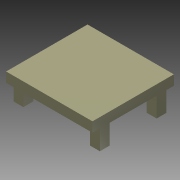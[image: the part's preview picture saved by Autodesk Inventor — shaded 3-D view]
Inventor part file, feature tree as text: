
AUTODESK INVENTOR PART (.ipt)
format: ipt  version: 2015 (Build 190159000, 159)  size: 593,408 bytes
history: native  units: in
note: dims shown in document units (in); Inventor stores cm internally (conversion verified against a paired STEP export)
features: thread x33, other x13, sketch x10, plane x6, projected_geometry x6, extrude x5, hole x4, mirror x3, pattern_circular x1, fillet x1, boolean_combine x1
ambient origin geometry x8: Origin, YZ Plane, XZ Plane, XY Plane, X Axis, Y Axis, Z Axis, Center Point
bodies: Solid6 (feature_tree)
feature tree (83):
  other  "board_with_hole_pipes.ipt"
  other  "Layout with const "
  plane  "Work Plane1"
  extrude  "Extrusion1"  Depth=18.0in
  extrude  "Extrusion2"  Depth=23.5in
  hole  "Hole1"  [1 undecoded]
  thread  "Thread1"  [1 undecoded]
  pattern_circular  "Circular Pattern1"  [2 undecoded]
  fillet  "Fillet1"  Radius=3.0in
  plane  "Work Plane3"
  hole  "Hole2"  [1 undecoded]
  thread  "Thread2"  [1 undecoded]
  thread  "Thread3"  [1 undecoded]
  thread  "Thread4"  [1 undecoded]
  thread  "Thread5"  [1 undecoded]
  thread  "Thread6"  [1 undecoded]
  thread  "Thread7"  [1 undecoded]
  mirror  "Mirror1"
  mirror  "Mirror2"
  mirror  "Mirror3"
  plane  "Work Plane4"
  extrude  "Extrusion3"  Depth=0.25in
  thread  "Thread8"  [1 undecoded]
  thread  "Thread9"  [1 undecoded]
  thread  "Thread10"  [1 undecoded]
  thread  "Thread11"  [1 undecoded]
  thread  "Thread12"  [1 undecoded]
  thread  "Thread13"  [1 undecoded]
  thread  "Thread14"  [1 undecoded]
  thread  "Thread15"  [1 undecoded]
  thread  "Thread16"  [1 undecoded]
  thread  "Thread17"  [1 undecoded]
  thread  "Thread18"  [1 undecoded]
  thread  "Thread19"  [1 undecoded]
  thread  "Thread20"  [1 undecoded]
  thread  "Thread21"  [1 undecoded]
  thread  "Thread22"  [1 undecoded]
  thread  "Thread23"  [1 undecoded]
  thread  "Thread24"  [1 undecoded]
  thread  "Thread25"  [1 undecoded]
  extrude  "Extrusion4"  Depth=0.25in TaperAngle=0.0deg
  plane  "Work Plane7"
  extrude  "Extrusion5"  Depth=0.25in TaperAngle=0.0deg
  boolean_combine  "Combine1"
  plane  "Work Plane8"
  plane  "Work Plane9"
  hole  "Hole3"  [1 undecoded]
  hole  "Hole4"  [1 undecoded]
  thread  "Thread26"  [1 undecoded]
  thread  "Thread27"  [1 undecoded]
  thread  "Thread28"  [1 undecoded]
  thread  "Thread29"  [1 undecoded]
  thread  "Thread30"  [1 undecoded]
  thread  "Thread31"  [1 undecoded]
  thread  "Thread32"  [1 undecoded]
  thread  "Thread33"  [1 undecoded]
  other  "Solid1::board_with_hole_pipes.ipt"
  other  "TaggingFeature1"
  sketch  "Sketch3"  dims[d0=0.1969in d1=18.0in]
  sketch  "Sketch4"  dims[d2=24.0in d3=23.5in]
  other  "legFL"
  sketch  "Sketch5"  dims[d4=17.5in d5=5.5in d6=1.5in]
  sketch  "Sketch6"  dims[d9=5.5in]
  sketch  "Sketch7"  dims[d10=1.5in]
  other  "Pattern of legFL:1"
  other  "legFR"
  other  "Pattern of legFL:2"
  other  "legBR"
  other  "Pattern of legFR:3"
  other  "legBL"
  sketch  "Sketch8"  dims[d11=5.5in]
  projected_geometry  "Projected Loop2"
  sketch  "Sketch10"  dims[d12=1.5in]
  sketch  "Sketch11"  dims[d15=4.0in]
  other  "miniplat"
  sketch  "Sketch12"  dims[d18=5.5in]
  projected_geometry  "Projected Loop3"
  projected_geometry  "Projected Loop4"
  projected_geometry  "Projected Loop5"
  projected_geometry  "Projected Loop6"
  projected_geometry  "Projected Loop7"
  sketch  "Sketch13"  dims[d19=1.5in d22=5.0in d23=3.0in d24=5.0in d25=3.0in d26=3.0in d27=3.0in d28=3.0in d29=5.0in d30=4.0in d31=3.5in d32=0.5in d33=1.0in d34=0.0in d35=0.0in d36=5.0in d37=0.5in d38=0.0in d39=0.25in d40=0.75in d41=0.375in d42=0.25in d43=0.5635in d44=1.8125in d45=0.8108in d46=1.0in d47=0.0in d48=2.3622in d49=360.0deg d51=0.4375in d52=0.25in d53=0.75in d54=0.375in d55=0.25in d56=0.5635in d57=1.8125in d58=0.8108in d59=1.0in d60=0.0in d61=1.0in d62=0.0in d63=1.0in d64=0.0in d65=1.0in d66=0.0in d67=1.0in d68=0.0in d69=1.0in d70=0.0in d71=3.475in d72=0.0in d73=1.0in d74=0.0in d75=1.0in d76=0.0in d77=1.0in d78=0.0in d79=1.0in d80=0.0in d81=1.0in d82=0.0in d83=1.0in d84=0.0in d85=1.0in d86=0.0in d87=1.0in d88=0.0in d89=1.0in d90=0.0in d91=1.0in d92=0.0in d93=1.0in d94=0.0in d95=1.0in d96=0.0in d97=1.0in d98=0.0in d99=1.0in d100=0.0in d101=1.0in d102=0.0in d103=1.0in d104=0.0in d105=1.0in d106=0.0in d107=1.0in d108=0.0in d109=1.0in d110=1.0in d111=1.0in d112=1.0in d113=1.0in d114=1.0in d115=2.0in d116=0.0in d117=1.0in d118=0.0in d119=0.5in d120=0.5in d121=0.5in d122=0.5in d123=0.5in d124=0.75in d125=0.375in d126=0.25in d127=0.5635in d128=2.0in d129=0.0in d130=0.5in d131=0.75in d132=0.375in d133=0.25in d134=0.5635in d135=2.0in d136=0.8108in d137=1.0in d138=0.0in d139=1.0in d140=0.0in d141=1.0in d142=0.0in d143=1.0in d144=0.0in d145=1.0in d146=0.0in d147=1.0in d148=0.0in d149=1.0in d150=0.0in d151=1.0in d152=0.0in]
  other  "platform"
note: 39 required parameter values undecoded (feature->parameter linkage not recoverable at this tier; creation-order binding heuristic only, values carry confidence <= 0.55)
